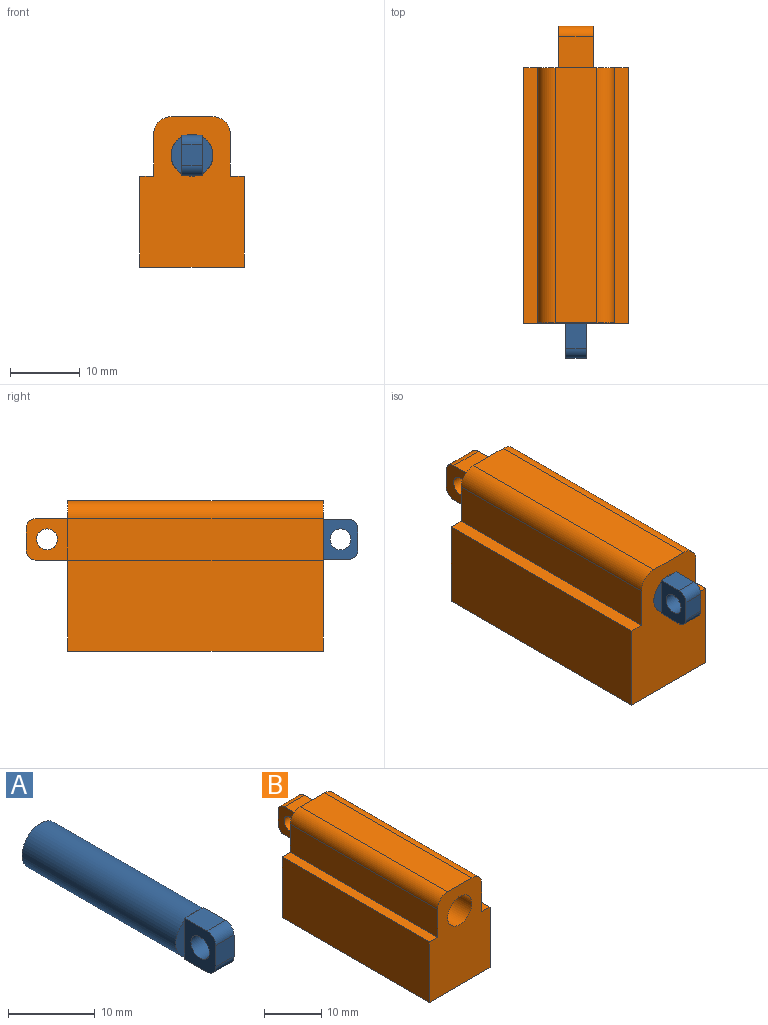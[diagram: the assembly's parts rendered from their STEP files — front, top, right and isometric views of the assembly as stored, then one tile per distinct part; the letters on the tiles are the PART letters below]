
ASSEMBLY  parts=2 mates=1
PART A: 18 faces, bbox 6x30x6 mm
  f0: plane 0.73x0.3mm, normal (0,1,0), area 0.1mm2, adj f3,f10,f15
  f1: plane 0.73x0.3mm, normal (0,1,0), area 0.1mm2, adj f5,f10,f15
  f2: plane 0.73x0.3mm, normal (0,1,0), area 0.1mm2, adj f5,f11,f15
  f3: plane 3.6x3mm, normal (0,0,-1), area 10.8mm2, adj f0,f4,f9,f10,f11,f14
  f4: plane 0.73x0.3mm, normal (0,1,0), area 0.1mm2, adj f3,f11,f15
  f5: plane 3.6x3mm, normal (0,0,1), area 10.8mm2, adj f1,f2,f6,f10,f11,f13
  f6: cylinder r=1.4mm len=3mm, axis (-1,0,0), area 6.6mm2, adj f5,f7,f10,f11
  f7: plane 3x3mm, normal (0,-1,0), area 9mm2, adj f6,f9,f10,f11
  f8: cylinder r=1.5mm len=3mm, axis (-1,0,0), area 28.3mm2, adj f10,f11
  f9: cylinder r=1.4mm len=3mm, axis (-1,0,0), area 6.6mm2, adj f3,f7,f10,f11
  f10: plane 5.8x5mm, normal (1,0,0), area 21.1mm2, adj f0,f1,f3,f5,f6,f7,f8,f9
  f11: plane 5.8x5mm, normal (-1,0,0), area 21.1mm2, adj f2,f3,f4,f5,f6,f7,f8,f9
  f12: plane 5.2x1.5mm, normal (0,-1,0), area 5.5mm2, adj f11,f15
  f13: plane 1.54x0.1mm, normal (0,-1,0), area 0.1mm2, adj f5,f15
  f14: plane 1.54x0.1mm, normal (0,-1,0), area 0.1mm2, adj f3,f15
  f15: cylinder r=3mm len=25mm, axis (0,-1,0), area 471.2mm2, adj f0,f1,f2,f4,f12,f13,f14,f16
  f16: plane 6x6mm, normal (0,1,0), area 28.3mm2, adj f15
  f17: plane 5.2x1.5mm, normal (0,-1,0), area 5.5mm2, adj f10,f15
PART B: 22 faces, bbox 15x42.5x21.5 mm
  f0: plane 21.5x15mm, normal (0,1,0), area 255.8mm2, adj f1,f2,f3,f4,f5,f6,f7,f8
  f1: plane 36.5x6mm, normal (-1,0,0), area 219mm2, adj f0,f2,f10,f12
  f2: plane 36.5x2mm, normal (0,0,1), area 73mm2, adj f0,f1,f3,f12
  f3: plane 36.5x13mm, normal (-1,0,0), area 474.5mm2, adj f0,f2,f4,f12
  f4: plane 36.5x15mm, normal (0,0,-1), area 547.5mm2, adj f0,f3,f5,f12
  f5: plane 36.5x13mm, normal (1,0,0), area 474.5mm2, adj f0,f4,f6,f12
  f6: plane 36.5x2mm, normal (0,0,1), area 73mm2, adj f0,f5,f7,f12
  f7: plane 36.5x6mm, normal (1,0,0), area 219mm2, adj f0,f6,f8,f12
  f8: cylinder r=2.5mm len=36.5mm, axis (0,1,0), area 143.3mm2, adj f0,f7,f9,f12
  f9: plane 36.5x6mm, normal (0,0,1), area 219mm2, adj f0,f8,f10,f12
  f10: cylinder r=2.5mm len=36.5mm, axis (0,1,0), area 143.3mm2, adj f0,f1,f9,f12
  f11: cylinder r=3mm len=26.5mm, axis (0,1,0), area 499.5mm2, adj f12,f13
  f12: plane 21.5x15mm, normal (0,-1,0), area 257.5mm2, adj f1,f2,f3,f4,f5,f6,f7,f8
  f13: plane 6x6mm, normal (0,-1,0), area 28.3mm2, adj f11
  f14: plane 5x4.5mm, normal (0,0,1), area 22.5mm2, adj f0,f19,f20,f21
  f15: plane 5x4.5mm, normal (0,0,-1), area 22.5mm2, adj f0,f16,f20,f21
  f16: cylinder r=1.5mm len=5mm, axis (-1,0,0), area 11.8mm2, adj f15,f17,f20,f21
  f17: plane 5x3mm, normal (0,1,0), area 15mm2, adj f16,f19,f20,f21
  f18: cylinder r=1.5mm len=5mm, axis (-1,0,0), area 47.1mm2, adj f20,f21
  f19: cylinder r=1.5mm len=5mm, axis (-1,0,0), area 11.8mm2, adj f14,f17,f20,f21
  f20: plane 6x6mm, normal (1,0,0), area 28mm2, adj f0,f14,f15,f16,f17,f18,f19
  f21: plane 6x6mm, normal (-1,0,0), area 28mm2, adj f0,f14,f15,f16,f17,f18,f19
PLACE A t=(-5.77,15.53,6.92)mm
PLACE B t=(-5.77,15.53,6.92)mm
MATE fastened B.f11 <-> A.f15  axis (0,1,0) through (-5.77,-7.72,6.92)mm
